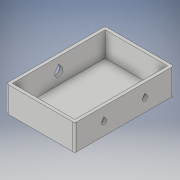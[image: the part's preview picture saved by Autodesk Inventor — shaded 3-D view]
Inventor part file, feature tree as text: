
AUTODESK INVENTOR PART (.ipt)
format: ipt  version: 2017 SP1 (Build 210196100, 196)  size: 194,048 bytes
history: native  units: in
note: dims shown in document units (in); Inventor stores cm internally (conversion verified against a paired STEP export)
features: sketch x7, extrude x4, projected_geometry x3, hole x2, chamfer x1, fillet x1
ambient origin geometry x8: Origin, YZ Plane, XZ Plane, XY Plane, X Axis, Y Axis, Z Axis, Center Point
bodies: Solid1 (feature_tree)
feature tree (18):
  extrude  "Extrusion1"  Depth=2.0in
  extrude  "Extrusion2"  Depth=0.6in
  sketch  "Sketch5"  dims[d4=0.6in d5=0.6in]
  hole  "Hole1"  [1 undecoded]
  hole  "Hole2"  [1 undecoded]
  chamfer  "Chamfer1"  Distance=1.5in
  fillet  "Fillet1"  Radius=2.704in
  extrude  "Extrusion3"  Depth=1.904in
  extrude  "Extrusion4"  Depth=0.125in
  sketch  "Sketch3"  dims[d0=3.0in d1=2.0in]
  sketch  "Sketch4"  dims[d2=0.6in d3=0.6in]
  projected_geometry  "Projected Loop1"
  projected_geometry  "Projected Loop2"
  sketch  "Sketch6"  dims[d6=0.85in d7=0.125in d8=0.0in]
  sketch  "Sketch7"  dims[d9=0.19in d10=1.5in d11=0.0in d12=2.704in]
  sketch  "Sketch8"  dims[d13=1.904in d14=1.904in]
  sketch  "Sketch9"  dims[d15=0.558in d16=0.431in d17=0.431in d18=0.558in d19=1.0in d20=0.8125in d21=0.8125in d22=1.775in d23=1.775in d24=2.5in d25=0.3in d26=0.75in d27=0.375in d28=0.25in d29=0.5635in d30=1.0in d31=0.8108in d32=0.8125in d33=0.8125in d34=3.025in d35=3.025in d36=0.5in d37=0.75in d38=0.375in d39=0.25in d40=0.5635in d41=1.0in d42=0.8108in d43=0.05in d44=0.125in d45=45.0deg d46=0.125in d47=0.3779in d48=1.0in d49=0.0in d50=0.3779in d51=1.0in d52=0.0in]
  projected_geometry  "Projected Loop3"
note: 2 required parameter values undecoded (feature->parameter linkage not recoverable at this tier; creation-order binding heuristic only, values carry confidence <= 0.55)
